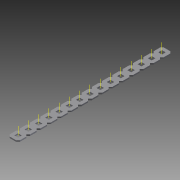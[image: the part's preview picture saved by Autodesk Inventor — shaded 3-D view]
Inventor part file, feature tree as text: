
AUTODESK INVENTOR PART (.ipt)
format: ipt  version: 2015 (Build 190159000, 159)  size: 1,154,560 bytes
history: native  units: in
note: dims shown in document units (in); Inventor stores cm internally (conversion verified against a paired STEP export)
features: other x24, extrude x2, pattern_linear x1, imported_body x1
ambient origin geometry x8: Origin, YZ Plane, XZ Plane, XY Plane, X Axis, Y Axis, Z Axis, Center Point
bodies: Body1 (feature_tree)
feature tree (28):
  other  "Diamond-Pattern"
  other  "Plate"
  extrude  "length cut"  TaperAngle=0.0deg  [1 undecoded]
  extrude  "width cut"  TaperAngle=0.0deg  [1 undecoded]
  other  "constraint axis"
  pattern_linear  "constraint axes"  Spacing1=0.5in  [1 undecoded]
  other  "front plane"
  other  "right plane"
  imported_body  "Base1"
  other  "length profile"
  other  "width profile"
  other  "Work Point1"
  other  "back plane"
  other  "left plane"
  other  "Work Axis170"
  other  "Work Axis171"
  other  "Work Axis172"
  other  "Work Axis173"
  other  "Work Axis174"
  other  "Work Axis175"
  other  "Work Axis176"
  other  "Work Axis177"
  other  "Work Axis178"
  other  "Work Axis179"
  other  "Work Axis180"
  other  "Work Axis181"
  other  "Work Axis182"
  other  "Work Axis183"
note: 3 required parameter values undecoded (feature->parameter linkage not recoverable at this tier; creation-order binding heuristic only, values carry confidence <= 0.55)
